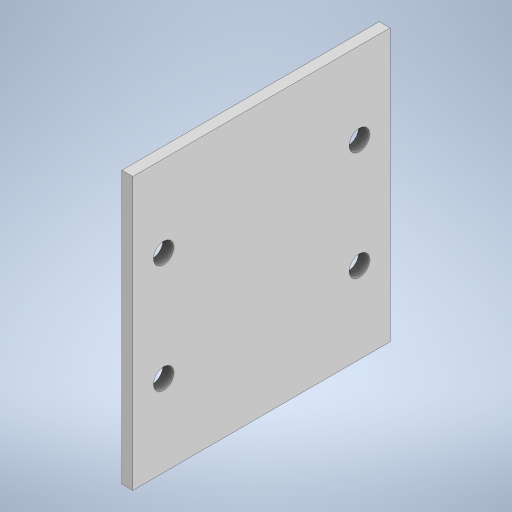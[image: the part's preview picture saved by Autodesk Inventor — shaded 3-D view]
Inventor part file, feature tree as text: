
AUTODESK INVENTOR PART (.ipt)
format: ipt  version: 2023 (Build 270158000, 158)  size: 221,696 bytes
history: native  units: in
note: dims shown in document units (in); Inventor stores cm internally (conversion verified against a paired STEP export)
features: extrude x1, sketch x1
ambient origin geometry x8: Origin, YZ Plane, XZ Plane, XY Plane, X Axis, Y Axis, Z Axis, Center Point
bodies: Solid1 (feature_tree)
feature tree (2):
  extrude  "Extrusion1"  Depth=0.71in
  sketch  "Sketch1"  dims[d0=0.5in d1=0.71in d2=0.75in d3=0.125in d4=0.2812in d5=0.0563in d9=0.54in d10=0.3in d11=0.3in d12=0.54in d13=0.1in d14=0.39in d15=0.125in d17=0.2in d18=0.03in d19=0.0in d20=0.085in]
